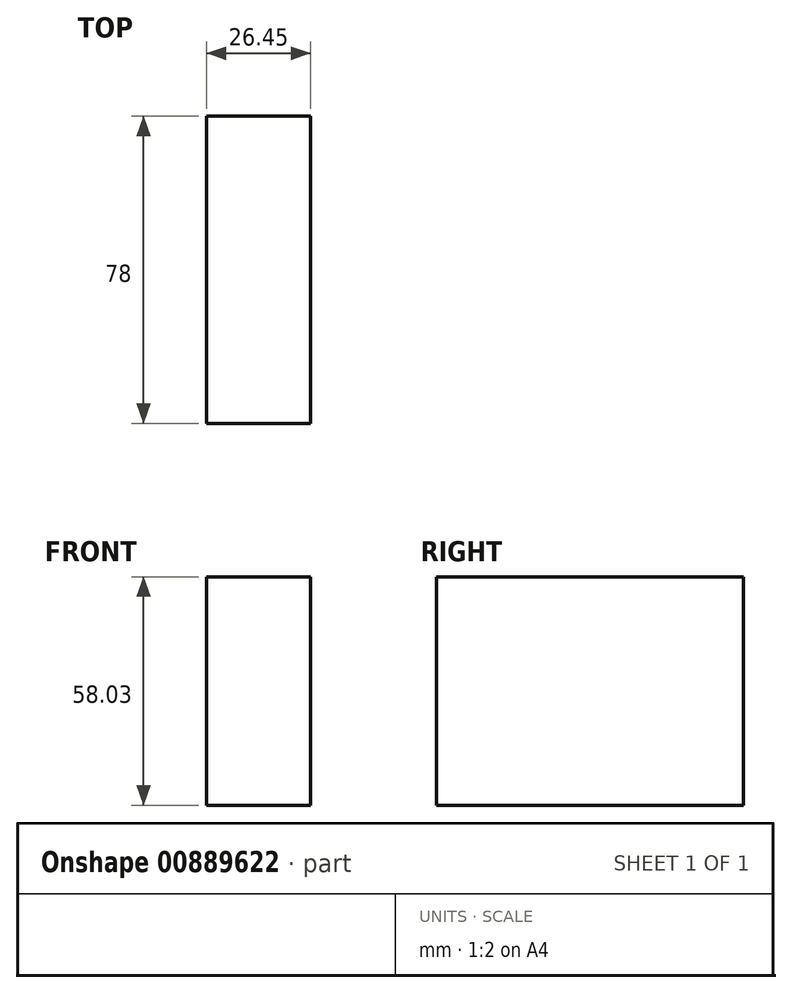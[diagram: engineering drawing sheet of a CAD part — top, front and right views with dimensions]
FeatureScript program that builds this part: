
annotation { "Feature Type Name" : "Feature", "Feature Type Description" : "" }
export const myFeature = defineFeature(function(context is Context, id is Id, definition is map)
    precondition{}
    {
        {
            var Q0;
            Q0=qCreatedBy(makeId("Front.planeOp"),FACE);
            var sketch = newSketch(context, id + "F0", { "sketchPlane" : qUnion([Q0])});
            skLineSegment(sketch, "E0.bottom", {"start": v(29.58, 30.83) * mm, "end": v(-29.58, 30.83) * mm});
            skLineSegment(sketch, "E0.top", {"start": v(29.58, -30.83) * mm, "end": v(-29.58, -30.83) * mm});
            skLineSegment(sketch, "E0.left", {"start": v(29.58, 30.83) * mm, "end": v(29.58, -30.83) * mm});
            skLineSegment(sketch, "E0.right", {"start": v(-29.58, 30.83) * mm, "end": v(-29.58, -30.83) * mm});
            skPoint(sketch, "E0.middle", {"position": v(0, 0) * mm});
            skLineSegment(sketch, "E1.bottom", {"start": v(21.76, -7.36) * mm, "end": v(2.01, -7.36) * mm});
            skLineSegment(sketch, "E1.top", {"start": v(21.76, -24.13) * mm, "end": v(2.01, -24.13) * mm});
            skLineSegment(sketch, "E1.left", {"start": v(21.76, -7.36) * mm, "end": v(21.76, -24.13) * mm});
            skLineSegment(sketch, "E1.right", {"start": v(2.01, -7.36) * mm, "end": v(2.01, -24.13) * mm});
            skPoint(sketch, "E1.middle", {"position": v(11.89, -15.75) * mm});
            skLineSegment(sketch, "E2.bottom", {"start": v(-29.58, 12.15) * mm, "end": v(-11.4, 12.15) * mm});
            skLineSegment(sketch, "E2.top", {"start": v(-29.58, 28.03) * mm, "end": v(-11.4, 28.03) * mm});
            skLineSegment(sketch, "E2.left", {"start": v(-29.58, 12.15) * mm, "end": v(-29.58, 28.03) * mm});
            skLineSegment(sketch, "E2.right", {"start": v(-11.4, 12.15) * mm, "end": v(-11.4, 28.03) * mm});
            skPoint(sketch, "E2.middle", {"position": v(-20.49, 20.09) * mm});
            skLineSegment(sketch, "E3.bottom", {"start": v(21.76, -7.36) * mm, "end": v(-4.7, -7.36) * mm});
            skLineSegment(sketch, "E3.top", {"start": v(21.76, 50.67) * mm, "end": v(-4.7, 50.67) * mm});
            skLineSegment(sketch, "E3.left", {"start": v(21.76, -7.36) * mm, "end": v(21.76, 50.67) * mm});
            skLineSegment(sketch, "E3.right", {"start": v(-4.7, -7.36) * mm, "end": v(-4.7, 50.67) * mm});
            skPoint(sketch, "E3.middle", {"position": v(8.53, 21.65) * mm});
            skSolve(sketch);
        }
        {
            var Q0;
            {var subQ0=sQuery(id+"F0.wireOp",EDGE,"E3.left");var subQ3=sQuery(id+"F0.wireOp",EDGE,"E0.bottom");var subQ4=makeQuery(id+"F0.imprint","INTERSECT",VERTEX,{"derivedFrom":[subQ3,subQ0]});Q0=makeQuery(id+"F0.imprint","IMPRINT",FACE,{"disambiguationData":[TD([[makeQuery(id+"F0.imprint","IMPRINT",EDGE,{"disambiguationData":[TD([[subQ4,-1.0]])],"derivedFrom":subQ3}),1.0]])]});}
            var Q1;
            {var subQ5=sQuery(id+"F0.wireOp",EDGE,"E3.top");Q1=makeQuery(id+"F0.imprint","IMPRINT",FACE,{"disambiguationData":[TD([[makeQuery(id+"F0.imprint","IMPRINT",EDGE,{"derivedFrom":subQ5}),1.0]])]});}
            extrude(context, id + "F1", {"entities" : qUnion([Q0, Q1]), "depth" : 78 * mm, "offsetDistance" : 25.4 * mm});
        }
    });
